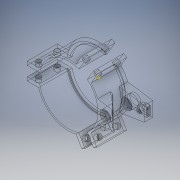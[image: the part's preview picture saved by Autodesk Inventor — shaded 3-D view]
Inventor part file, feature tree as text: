
AUTODESK INVENTOR PART (.ipt)
format: ipt  version: 2017 (Build 210142000, 142)  size: 407,040 bytes
history: native  units: mm
features: sketch x13, extrude x12, projected_geometry x6, chamfer x1
ambient origin geometry x8: Origin, YZ Plane, XZ Plane, XY Plane, X Axis, Y Axis, Z Axis, Center Point
bodies: Solid1 (feature_tree)
feature tree (32):
  extrude  "Extrusion1"  Depth=50.0mm
  extrude  "Extrusion2"  Depth=24.0mm TaperAngle=0.0deg
  sketch  "Sketch3"  dims[d5=7.833333mm d6=30.0mm d8=360.0deg]
  extrude  "Extrusion3"  Depth=7.833333mm TaperAngle=360.0deg
  extrude  "Extrusion4"  Depth=10.0mm
  extrude  "Extrusion5"  Depth=3.0mm TaperAngle=360.0deg
  extrude  "Extrusion6"  Depth=24.0mm
  extrude  "Extrusion7"  Depth=3.8mm
  extrude  "Extrusion8"  Depth=24.0mm TaperAngle=0.0deg
  extrude  "Extrusion9"  Depth=24.0mm TaperAngle=0.0deg
  extrude  "Extrusion10"  Depth=24.0mm TaperAngle=0.0deg
  extrude  "Extrusion11"  Depth=2.9mm
  chamfer  "Chamfer1"  Distance=2.0mm
  extrude  "Extrusion12"  Depth=2.0mm TaperAngle=0.0deg
  sketch  "Sketch1"  dims[d0=47.0mm d1=50.0mm]
  sketch  "Sketch2"  dims[d2=3.916667mm d3=24.0mm d4=0.0mm]
  sketch  "Sketch4"  dims[d10=25.0mm d11=0.0mm d12=10.0mm]
  sketch  "Sketch6"  dims[d13=3.0mm d14=30.0mm d16=360.0deg]
  projected_geometry  "Projected Loop3"
  sketch  "Sketch7"  dims[d18=24.0mm d19=0.0mm d29=4.5mm]
  sketch  "Sketch8"  dims[d30=4.5mm d31=3.8mm]
  sketch  "Sketch9"  dims[d32=3.8mm d33=24.0mm d34=12.0mm d35=0.0mm d36=0.0mm]
  projected_geometry  "Projected Loop4"
  sketch  "Sketch10"  dims[d37=4.5mm d38=4.5mm d39=3.8mm d40=3.8mm d41=24.0mm d42=12.0mm d43=0.0mm d44=0.0mm]
  sketch  "Sketch11"  dims[d45=4.5mm d46=4.5mm d47=3.8mm d48=3.8mm d49=24.0mm d50=12.0mm d51=0.0mm d52=0.0mm]
  sketch  "Sketch12"  dims[d57=2.0mm d58=0.0mm d63=3.8mm d70=2.0mm d75=2.9mm d76=0.0mm]
  projected_geometry  "Projected Loop8"
  projected_geometry  "Projected Loop9"
  projected_geometry  "Projected Loop10"
  sketch  "Sketch13"  dims[d83=2.0mm d84=0.0mm d86=2.0mm d87=0.0mm]
  projected_geometry  "Projected Loop11"
  sketch  "Sketch14"  dims[d93=8.7mm d96=5.0mm d99=3.8mm d101=5.0mm d102=3.8mm d103=8.7mm d104=5.0mm d105=43.0mm d106=43.0mm d107=10.0mm d108=0.0mm d109=10.725mm d110=10.0mm d111=45.0deg d112=100.0mm d113=0.0mm d118=0.016443mm d119=0.872665mm d120=0.872665mm]
